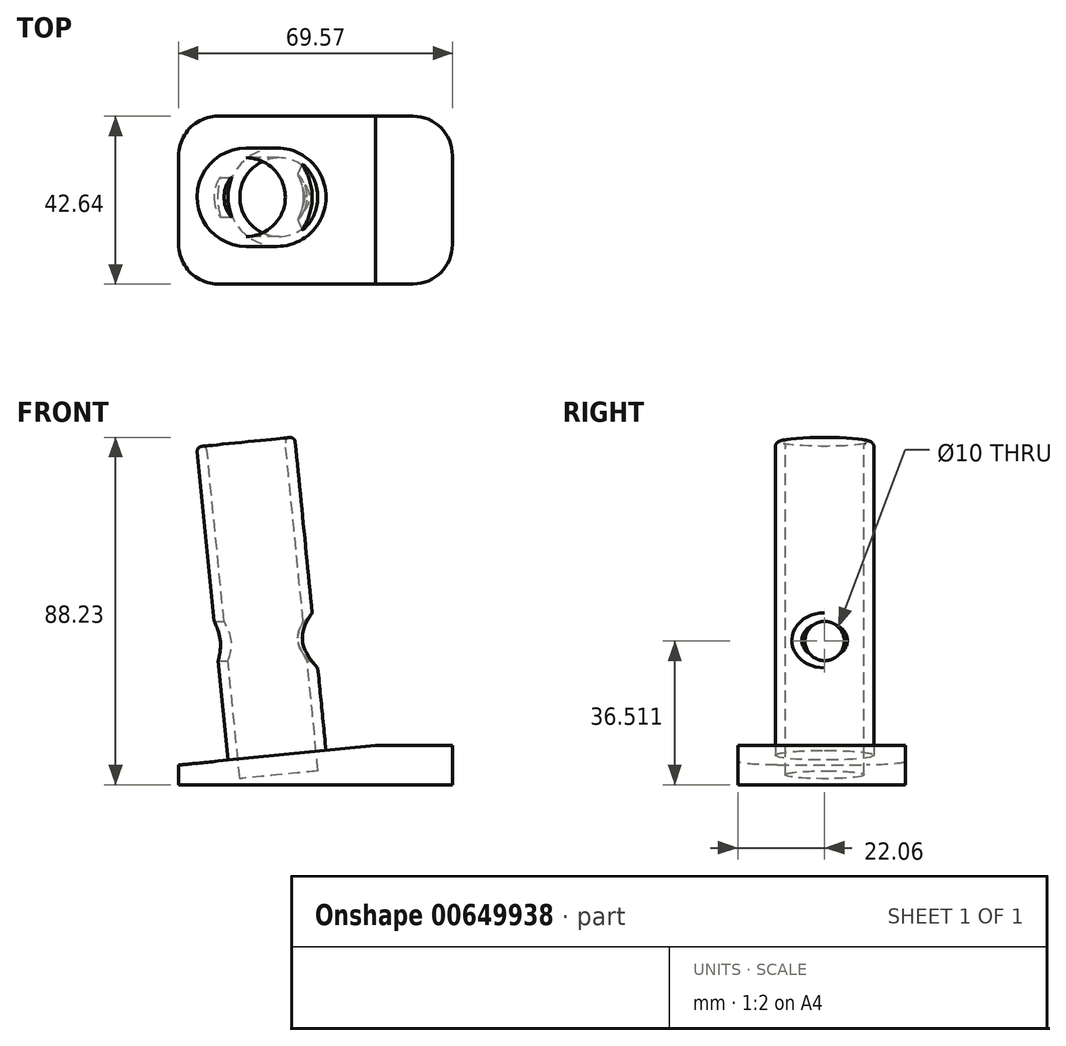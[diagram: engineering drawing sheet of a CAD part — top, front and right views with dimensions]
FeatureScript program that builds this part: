
annotation { "Feature Type Name" : "Feature", "Feature Type Description" : "" }
export const myFeature = defineFeature(function(context is Context, id is Id, definition is map)
    precondition{}
    {
        {
            var Q0;
            Q0=qCreatedBy(makeId("Top.planeOp"),FACE);
            var sketch = newSketch(context, id + "F0", { "sketchPlane" : qUnion([Q0])});
            skLineSegment(sketch, "E0.bottom", {"start": v(-37.15, 20.58) * mm, "end": v(32.42, 20.58) * mm});
            skLineSegment(sketch, "E0.top", {"start": v(-37.15, -22.06) * mm, "end": v(32.42, -22.06) * mm});
            skLineSegment(sketch, "E0.left", {"start": v(-37.15, 20.58) * mm, "end": v(-37.15, -22.06) * mm});
            skLineSegment(sketch, "E0.right", {"start": v(32.42, 20.58) * mm, "end": v(32.42, -22.06) * mm});
            skSolve(sketch);
        }
        {
            var Q0;
            Q0 = qSketchRegion(id + "F0", true);
            extrude(context, id + "F1", {"entities" : qUnion([Q0]), "depth" : 10 * mm, "offsetDistance" : 25 * mm});
        }
        {
            var Q0;
            Q0=makeQuery(id+"F1.opExtrude","CAP_EDGE",EDGE,{"disambiguationData":[OSD([sQuery(id+"F0.wireOp",EDGE,"E0.left")])],"isStart":false});
            chamfer(context, id + "F2", {"entities" : qUnion([Q0]), "chamferType" : ChamferType.TWO_OFFSETS, "width1" : 5 * mm, "oppositeDirection" : true, "width2" : 50 * mm, "tangentPropagation" : true});
        }
        {
            var Q0;
            Q0=makeQuery(id+"F2.opChamfer","BLEND_FACE",FACE,{"disambiguationData":[OSD([sQuery(id+"F0.wireOp",EDGE,"E0.left")])]});
            var sketch = newSketch(context, id + "F3", { "sketchPlane" : qUnion([Q0])});
            skCircle(sketch, "E1", {"center": v(-11.35, 0) * mm, "radius": 12.5 * mm});
            skLineSegment(sketch, "E2", {"start": v(-36.47, 0) * mm, "end": v(13.78, 0) * mm, "construction": true});
            skCircle(sketch, "E3", {"center": v(-11.35, 0) * mm, "radius": 10 * mm});
            skSolve(sketch);
        }
        {
            var Q0;
            Q0=makeQuery(id+"F3.imprint","IMPRINT",FACE,{"disambiguationData":[TD([[makeQuery(id+"F3.imprint","IMPRINT",EDGE,{"derivedFrom":sQuery(id+"F3.wireOp",EDGE,"E3")}),1.0]])]});
            extrude(context, id + "F4", {"entities" : qUnion([Q0]), "operationType" : NewBodyOperationType.REMOVE, "oppositeDirection" : true, "depth" : 5 * mm, "offsetDistance" : 25 * mm});
        }
        {
            var Q0;
            Q0=makeQuery(id+"F3.imprint","IMPRINT",FACE,{"disambiguationData":[TD([[makeQuery(id+"F3.imprint","IMPRINT",EDGE,{"derivedFrom":sQuery(id+"F3.wireOp",EDGE,"E1")}),1.0]])]});
            extrude(context, id + "F5", {"entities" : qUnion([Q0]), "operationType" : NewBodyOperationType.ADD, "depth" : 80 * mm, "offsetDistance" : 25 * mm});
        }
        {
            var Q0;
            Q0=makeQuery(id+"F5.opExtrude","CAP_EDGE",EDGE,{"disambiguationData":[OSD([sQuery(id+"F3.wireOp",EDGE,"E1")])],"isStart":false});
            var Q1;
            Q1=makeQuery(id+"F5.opExtrude","CAP_EDGE",EDGE,{"disambiguationData":[OSD([sQuery(id+"F3.wireOp",EDGE,"E3")])],"isStart":false});
            fillet(context, id + "F6", {"entities" : qUnion([Q0, Q1]), "radius" : 1.25 * mm, "tangentPropagation" : true, "allowEdgeOverflow" : false});
        }
        {
            var Q0;
            Q0=makeQuery(id+"F1.opExtrude","SWEPT_EDGE",EDGE,{"disambiguationData":[OSD([sQuery(id+"F0.wireOp",EDGE,"E0.top"),sQuery(id+"F0.wireOp",EDGE,"E0.right")])]});
            var Q1;
            Q1=makeQuery(id+"F1.opExtrude","SWEPT_EDGE",EDGE,{"disambiguationData":[OSD([sQuery(id+"F0.wireOp",EDGE,"E0.bottom"),sQuery(id+"F0.wireOp",EDGE,"E0.right")])]});
            var Q2;
            Q2=makeQuery(id+"F1.opExtrude","SWEPT_EDGE",EDGE,{"disambiguationData":[OSD([sQuery(id+"F0.wireOp",EDGE,"E0.bottom"),sQuery(id+"F0.wireOp",EDGE,"E0.left")])]});
            var Q3;
            Q3=makeQuery(id+"F1.opExtrude","SWEPT_EDGE",EDGE,{"disambiguationData":[OSD([sQuery(id+"F0.wireOp",EDGE,"E0.top"),sQuery(id+"F0.wireOp",EDGE,"E0.left")])]});
            fillet(context, id + "F7", {"entities" : qUnion([Q0, Q1, Q2, Q3]), "radius" : 10 * mm, "tangentPropagation" : true, "allowEdgeOverflow" : false});
        }
        {
            var Q0;
            Q0=qCreatedBy(makeId("Right.planeOp"),FACE);
            var sketch = newSketch(context, id + "F8", { "sketchPlane" : qUnion([Q0])});
            skCircle(sketch, "E4", {"center": v(0, 36.51) * mm, "radius": 5 * mm});
            skSolve(sketch);
        }
        {
            var Q0;
            Q0=makeQuery(id+"F8.imprint","IMPRINT",FACE,{"disambiguationData":[TD([[makeQuery(id+"F8.imprint","IMPRINT",EDGE,{"derivedFrom":sQuery(id+"F8.wireOp",EDGE,"E4")}),1.0]])]});
            extrude(context, id + "F9", {"entities" : qUnion([Q0]), "operationType" : NewBodyOperationType.REMOVE, "oppositeDirection" : true, "depth" : 39.7 * mm, "offsetDistance" : 25 * mm});
        }
        {
            var Q0;
            Q0=makeQuery(id+"F9.boolean.opBoolean","INTERSECT",EDGE,{"disambiguationData":[OD(1.0)],"derivedFrom":[makeQuery(id+"F5.opExtrude","SWEPT_FACE",FACE,{"disambiguationData":[OSD([sQuery(id+"F3.wireOp",EDGE,"E1")])]}),makeQuery(id+"F9.opExtrude","SWEPT_FACE",FACE,{"disambiguationData":[OSD([sQuery(id+"F8.wireOp",EDGE,"E4")])]})]});
            chamfer(context, id + "F10", {"entities" : qUnion([Q0]), "width" : 2 * mm, "tangentPropagation" : true});
        }
    });
